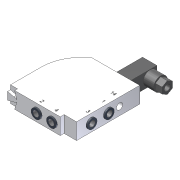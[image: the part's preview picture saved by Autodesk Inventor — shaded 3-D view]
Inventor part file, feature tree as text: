
AUTODESK INVENTOR PART (.ipt)
format: ipt  version: unknown  size: 317,440 bytes
history: native  units: mm (DEFAULTED — no unit token found)
features: extrude x14, sketch x14
ambient origin geometry x8: Origin, YZ Plane, XZ Plane, XY Plane, X Axis, Y Axis, Z Axis, Center Point
feature tree (28):
  extrude  "Extrusion10"  Depth=70.0mm
  extrude  "Extrusion11"  Depth=50.0mm
  extrude  "Extrusion12"  Depth=13.0mm
  sketch  "Sketch12"  dims[d71=17.0mm d72=0.0mm d73=15.0mm]
  extrude  "Extrusion13"  Depth=15.0mm
  extrude  "Extrusion14"  Depth=10.0mm
  extrude  "Extrusion15"  Depth=6.0mm TaperAngle=0.0deg
  extrude  "Extrusion16"  Depth=0.75mm
  extrude  "Extrusion17"  Depth=3.0mm
  extrude  "Extrusion18"  Depth=9.0mm TaperAngle=0.0deg
  sketch  "Sketch17"  dims[d84=7.0mm d85=0.0mm d86=9.0mm d87=0.0mm]
  extrude  "Extrusion19"  Depth=1.5mm TaperAngle=0.0deg
  extrude  "Extrusion20"  Depth=1.5mm TaperAngle=0.0deg
  extrude  "Extrusion21"  Depth=33.0mm
  extrude  "Extrusion22"  Depth=24.0mm
  extrude  "Extrusion23"  Depth=2.0mm
  sketch  "Sketch1"  dims[d65=68.0mm d66=70.0mm]
  sketch  "Sketch10"  dims[d67=35.0mm d68=50.0mm]
  sketch  "Sketch11"  dims[d69=4.0mm d70=13.0mm]
  sketch  "Sketch13"  dims[d74=15.0mm d75=10.0mm]
  sketch  "Sketch14"  dims[d76=3.0mm d77=0.0mm d78=6.0mm d79=0.0mm]
  sketch  "Sketch15"  dims[d80=3.0mm d81=0.75mm]
  sketch  "Sketch16"  dims[d82=2.0mm d83=3.0mm]
  sketch  "Sketch18"  dims[d88=10.0mm d89=1.5mm d90=0.0mm]
  sketch  "Sketch20"  dims[d91=10.0mm d92=1.5mm d93=0.0mm]
  sketch  "Sketch21"  dims[d94=15.0mm d95=33.0mm]
  sketch  "Sketch22"  dims[d96=8.0mm d97=24.0mm]
  sketch  "Sketch23"  dims[d98=2.0mm d99=2.0mm d100=6.5mm d101=7.0mm d102=0.0mm d103=45.0mm d106=2.0mm d107=2.0mm d108=7.0mm d109=0.0mm d110=3.0mm d111=0.0mm d112=8.0mm d113=14.0mm d114=25.0mm d115=0.0mm d116=11.0mm d117=0.0mm d118=7.0mm d119=0.0mm d120=8.0mm d121=0.0mm]
